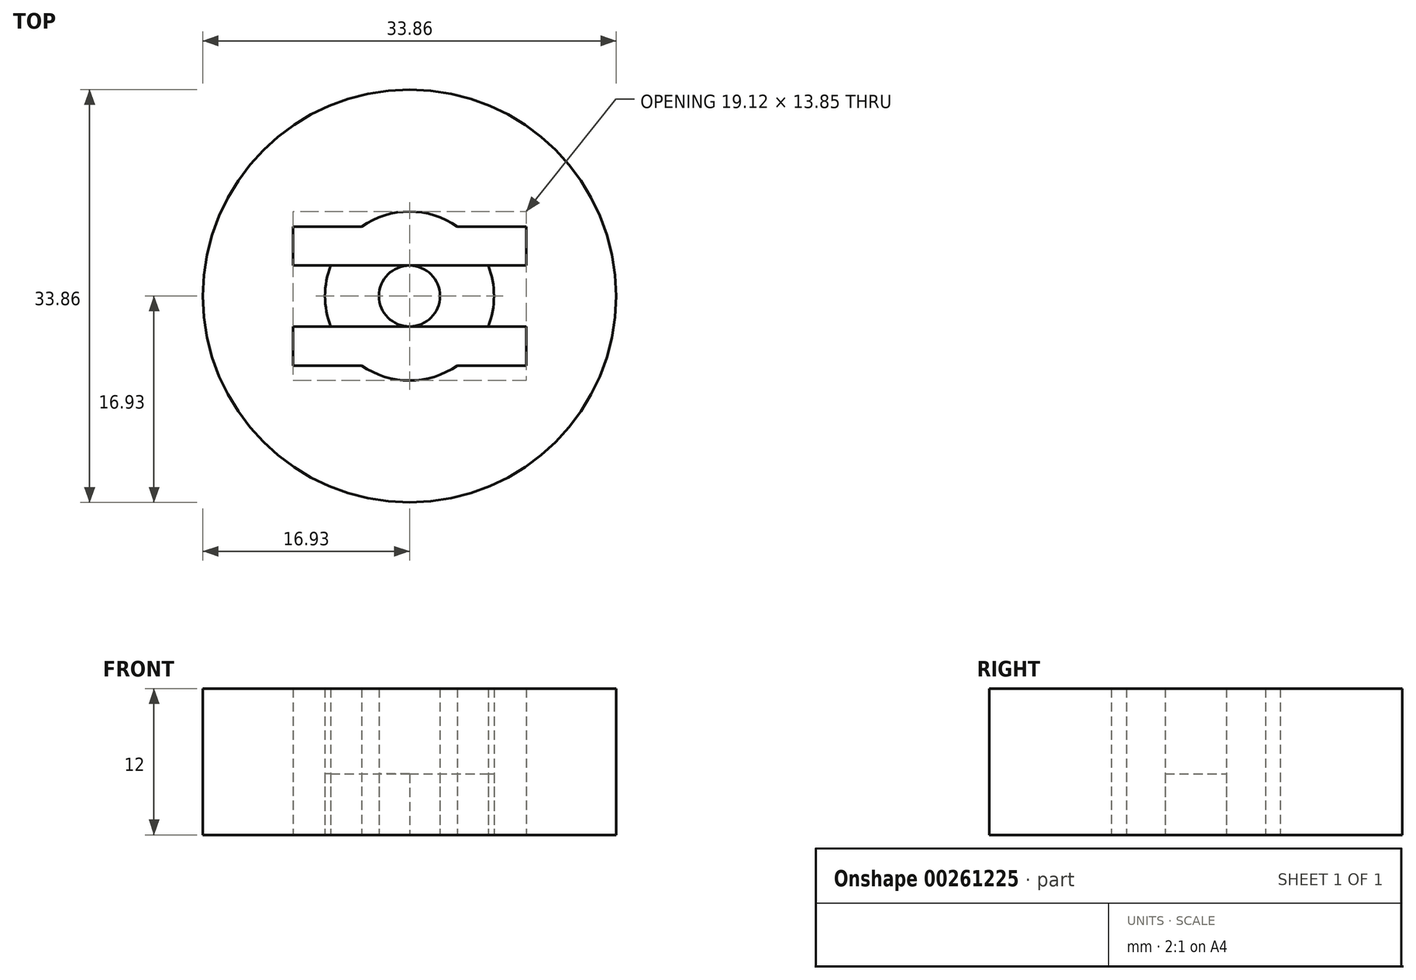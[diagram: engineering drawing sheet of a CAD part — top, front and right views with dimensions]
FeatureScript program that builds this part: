
annotation { "Feature Type Name" : "Feature", "Feature Type Description" : "" }
export const myFeature = defineFeature(function(context is Context, id is Id, definition is map)
    precondition{}
    {
        {
            var Q0;
            Q0=qCreatedBy(makeId("Top.planeOp"),FACE);
            var sketch = newSketch(context, id + "F0", { "sketchPlane" : qUnion([Q0])});
            skArc(sketch, "E0", {"start": v(3.93, 5.7) * mm, "mid": v(0, 6.92) * mm, "end": v(-3.93, 5.7) * mm});
            skCircle(sketch, "E1.0", {"center": v(0, 0) * mm, "radius": 16.92 * mm});
            skCircle(sketch, "E2", {"center": v(0, 0) * mm, "radius": 2.5 * mm});
            skLineSegment(sketch, "E3", {"start": v(-9.56, 2.5) * mm, "end": v(9.56, 2.5) * mm});
            skLineSegment(sketch, "E4", {"start": v(-9.56, -2.5) * mm, "end": v(9.56, -2.5) * mm});
            skLineSegment(sketch, "E5.0", {"start": v(3.93, 5.7) * mm, "end": v(9.56, 5.7) * mm});
            skLineSegment(sketch, "E6.0", {"start": v(3.93, -5.7) * mm, "end": v(9.56, -5.7) * mm});
            skLineSegment(sketch, "E7", {"start": v(9.56, 5.7) * mm, "end": v(9.56, 2.5) * mm});
            skLineSegment(sketch, "E8", {"start": v(0, 0) * mm, "end": v(0, 8.62) * mm, "construction": true});
            skPoint(sketch, "E9.orphan", {"position": v(6.46, 2.5) * mm});
            skLineSegment(sketch, "E10.trimOffspring", {"start": v(9.56, -2.5) * mm, "end": v(9.56, -5.7) * mm});
            skLineSegment(sketch, "E11.MirrorCS", {"start": v(-3.93, 5.7) * mm, "end": v(-9.56, 5.7) * mm});
            skLineSegment(sketch, "E12.MirrorCS", {"start": v(-9.56, 5.7) * mm, "end": v(-9.56, 2.5) * mm});
            skLineSegment(sketch, "E13.MirrorCS", {"start": v(-9.56, -2.5) * mm, "end": v(-9.56, -5.7) * mm});
            skLineSegment(sketch, "E14.MirrorCS", {"start": v(-3.93, -5.7) * mm, "end": v(-9.56, -5.7) * mm});
            skPoint(sketch, "E15.orphan", {"position": v(-3.93, 5.7) * mm});
            skPoint(sketch, "E16.orphan", {"position": v(-9.56, 5.7) * mm});
            skArc(sketch, "E17.trimOffspring", {"start": v(-6.46, 2.5) * mm, "mid": v(-6.92, 0) * mm, "end": v(-6.46, -2.5) * mm});
            skArc(sketch, "E18.trimOffspring", {"start": v(-3.93, -5.7) * mm, "mid": v(0, -6.93) * mm, "end": v(3.93, -5.7) * mm});
            skArc(sketch, "E19.trimOffspring", {"start": v(6.46, -2.5) * mm, "mid": v(6.92, 0) * mm, "end": v(6.46, 2.5) * mm});
            skSolve(sketch);
        }
        {
            var Q0;
            Q0=makeQuery(id+"F0.imprint","IMPRINT",FACE,{"disambiguationData":[TD([[makeQuery(id+"F0.imprint","IMPRINT",EDGE,{"derivedFrom":sQuery(id+"F0.wireOp",EDGE,"E1.0")}),1.0]])]});
            extrude(context, id + "F1", {"entities" : qUnion([Q0]), "depth" : 12 * mm});
        }
        {
            var Q0;
            {var subQ5=sQuery(id+"F0.wireOp",EDGE,"E19.trimOffspring");Q0=makeQuery(id+"F0.imprint","IMPRINT",FACE,{"disambiguationData":[TD([[makeQuery(id+"F0.imprint","IMPRINT",EDGE,{"derivedFrom":subQ5}),1.0]])]});}
            var Q1;
            {var subQ5=sQuery(id+"F0.wireOp",EDGE,"E17.trimOffspring");Q1=makeQuery(id+"F0.imprint","IMPRINT",FACE,{"disambiguationData":[TD([[makeQuery(id+"F0.imprint","IMPRINT",EDGE,{"derivedFrom":subQ5}),1.0]])]});}
            extrude(context, id + "F2", {"entities" : qUnion([Q0, Q1]), "depth" : 5 * mm});
        }
        {
            var Q0;
            {var subQ0=sQuery(id+"F0.wireOp",EDGE,"E2");var subQ1=makeQuery(id+"F0.imprint","INTERSECT",VERTEX,{"derivedFrom":[subQ0,sQuery(id+"F0.wireOp",EDGE,"E3")]});Q0=makeQuery(id+"F0.imprint","IMPRINT",FACE,{"disambiguationData":[TD([[makeQuery(id+"F0.imprint","IMPRINT",EDGE,{"disambiguationData":[TD([[subQ1,-1.0]])],"derivedFrom":subQ0}),1.0]])]});}
            extrude(context, id + "F3", {"entities" : qUnion([Q0]), "depth" : 12 * mm});
        }
    });
